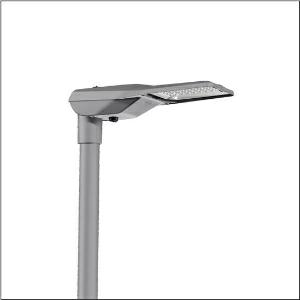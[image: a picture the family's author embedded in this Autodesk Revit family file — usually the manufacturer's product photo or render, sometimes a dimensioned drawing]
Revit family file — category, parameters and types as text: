
# Revit family: streetlight_sl_21_mini___stw1_0a_5xe2e23t08hb_3503
name_source: partatom
category: Lighting Fixtures
units: mm (PartAtom-declared; Revit-internal decimal feet)

## family parameters
Cut with Voids When Loaded = No
Host = Face
Light Source = No
Part Type = Normal
Room Calculation Point = No
Round Connector Dimension = Use Diameter
Shared = No

## types (1)
- --- (1 x LED, 7490 lm, 66 W, 2200K)
    Apparent Load = 66 VA
    CIE Flux Codes = 38 75 98 100 100
    Color Rendering = 70
    Color Temperature = 2200K
    Default Elevation = 1800 mm
    Description = Streetlight SL 21 mini, mast luminaire, primary light control with lens, of PMMA, primary optical cover: cover, of toughened safety glass, transparent, light distribution: STW1.0a, light emission: direct distribution, primary light characteristic: asymmetric, installation type: side-entry, post-top, LED, High Power LED, rated luminous flux: 7.490lm, luminous efficacy: 114lm/W, light colour: 722, colour temperature: 2200K, control gear: D4i, control: overheat protection, constant luminous flux control, time-dependent luminous flux control, flexible luminous flux parameterisation, pre-setting: logarithmic dimming characteristic, mains connection: 220..240V, AC, 50/60Hz, start of lifetime: 66W, end of service life: 69W, reduction: 30W, luminaire housing, of diecast aluminium, powder-coated, SITECO metallic grey (DB 702S), corrosivity category C5 high according to DIN EN ISO 12944, please order mast flange separately, inclination adjustable: 0°, 5°, 10°, 15°, sealing non-destructively replaceable, multi-level sealing system, length: 628mm, width: 235mm, height: 110mm, mast flange for spigot size: 42mm (side-entry): 5XC10008XM4, 60/48mm (side-entry/post-top): 5XC10108XM2, 76/60mm (side-entry/post-top): 5XC10108XM1, mounting height: 4..8m, Smart Interface below and above, protection rating (complete): IP66, insulation class (complete): insulation class II (safety insulation), certification: CE, ENEC, ENEC+, VDE, impact resistance: IK10, permissible operating ambient temperature for outdoor applications: -40..+50°C, standard-compliant lighting for roads and squares, packaging unit: 1 piece

Light Distribution: STW1.0a
    Height = 110 mm
    Lamp = 1 x LED
    Lamp Light Flux = 7490 lm
    Lamp Power = 66 W
    Lamp count = 1
    Length = 625 mm
    Luminous efficacy = 113 lm/W
    Manufacturer = Siteco
    ModVariant = No
    Model = 5XE2E23T08HB
    Mounting Place = Pole
    Mounting Type = Pole top
    Number of Poles = 1
    OnlyDefault = Yes
    Power Factor = 1
    Product Name = Streetlight SL 21 mini | STW1.0a
    Product group = mast luminaire | pylon top
    ProductGroupID = 6100
    Protection Class = Protection class II
    Protection Degree = IP 66
    RLX_Detail_Level = 1
    RLX_Emergency_Light_Flux = 0 lm
    RLX_Emergency_Type = 0
    RLX_Emergency_Type_DB = No
    RlxData = <blob elided: 26353 chars, md5=5cb38a69>
    Socket = socket
    Standby Power = 0 W
    System Light Flux = 7490 lm
    System Power = 66 W
    Type Comments = factory setting: luminous flux: 100 % | dim-lin: 254 | 670 mA
    Type Image = l_1003514.jpg
    URL = http://relux.com
    VarID = @adj_186243
    Voltage = 0 V
    Weight = 0.00 kg
    Width = 234 mm

## geometry (parser evidence)
native form markers: Blend x4, Sweep x10
no freeform markers — native parametric forms only
